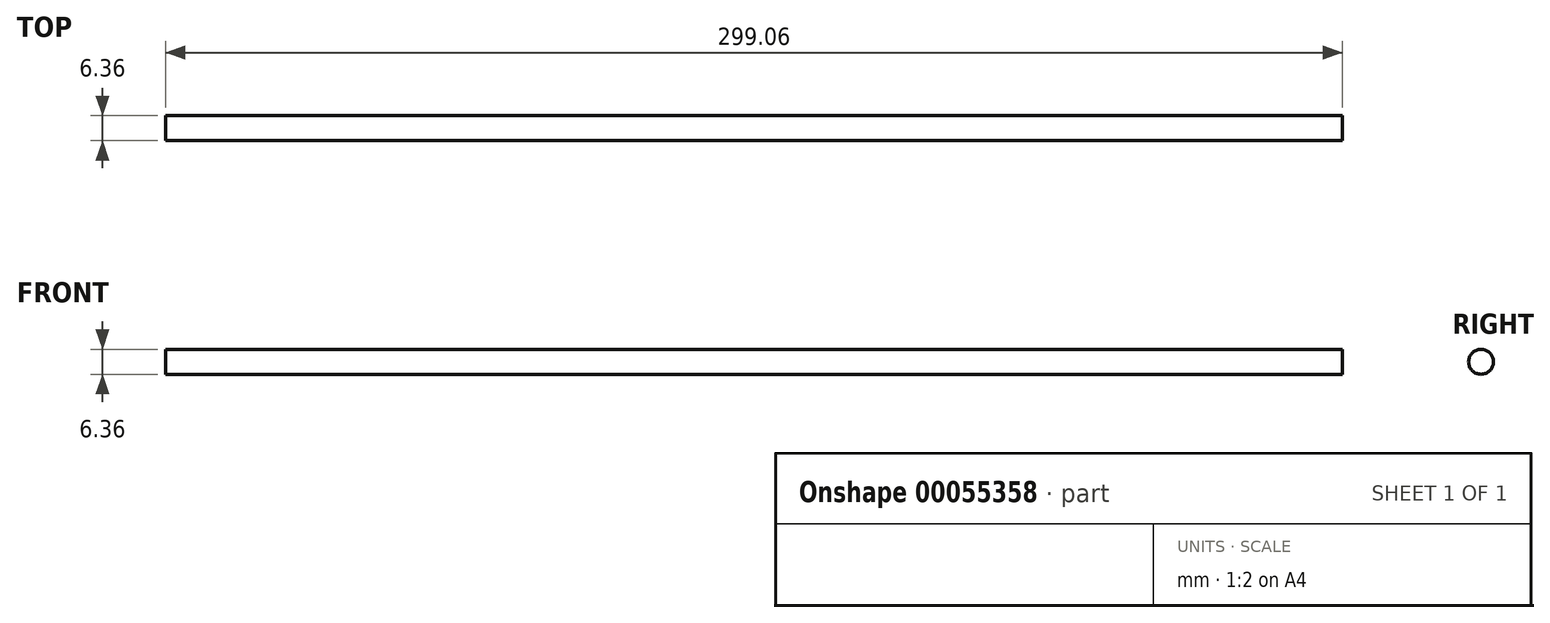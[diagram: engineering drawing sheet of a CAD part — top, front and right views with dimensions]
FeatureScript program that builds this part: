
annotation { "Feature Type Name" : "Feature", "Feature Type Description" : "" }
export const myFeature = defineFeature(function(context is Context, id is Id, definition is map)
    precondition{}
    {
        {
            var Q0;
            Q0=qCreatedBy(makeId("Right.planeOp"),FACE);
            var sketch = newSketch(context, id + "F0", { "sketchPlane" : qUnion([Q0])});
            skCircle(sketch, "E0", {"center": v(0, 0) * mm, "radius": 3.18 * mm});
            skSolve(sketch);
        }
        {
            var Q0;
            Q0=qSketchRegion(id+"F0",true);
            extrude(context, id + "F1", {"entities" : qUnion([Q0]), "endBound" : BoundingType.SYMMETRIC, "depth" : 299.06 * mm});
        }
    });
